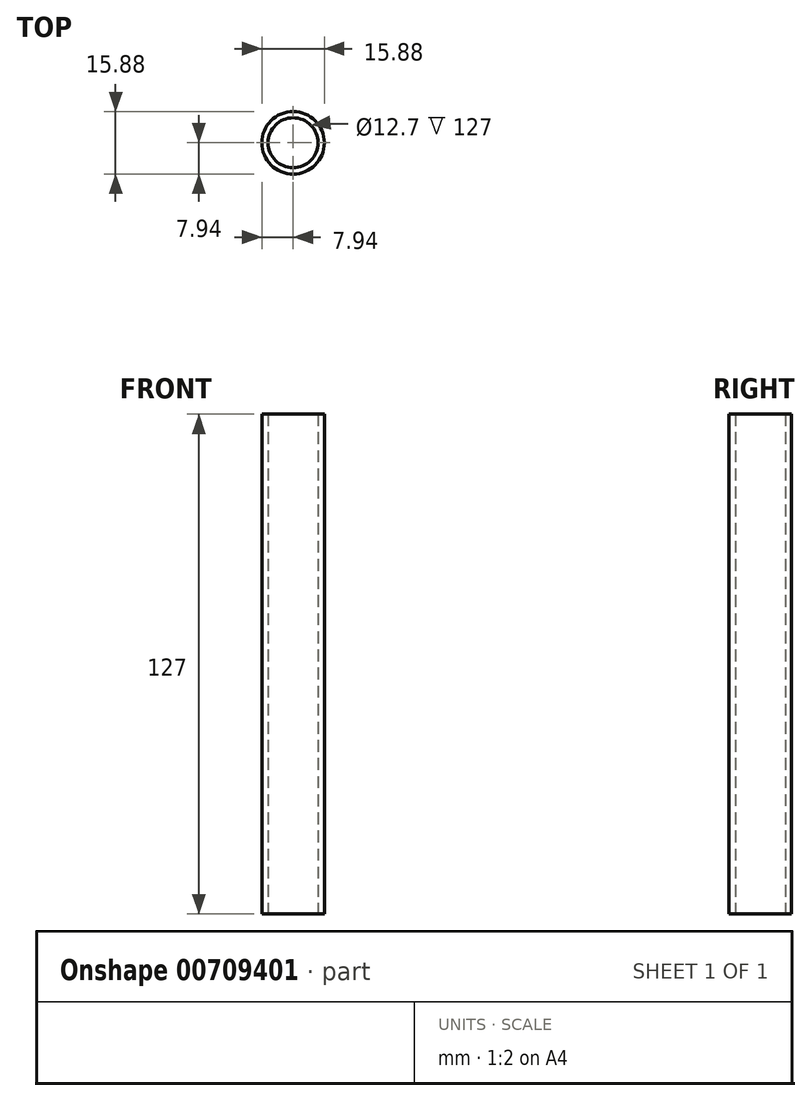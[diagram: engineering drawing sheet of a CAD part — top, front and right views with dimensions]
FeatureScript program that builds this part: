
annotation { "Feature Type Name" : "Feature", "Feature Type Description" : "" }
export const myFeature = defineFeature(function(context is Context, id is Id, definition is map)
    precondition{}
    {
        {
            var Q0;
            Q0=qCreatedBy(makeId("Top.planeOp"),FACE);
            var sketch = newSketch(context, id + "F0", { "sketchPlane" : qUnion([Q0])});
            skLineSegment(sketch, "E0", {"start": v(0, 0) * mm, "end": v(6.35, 0) * mm});
            skCircle(sketch, "E1", {"center": v(0, 0) * mm, "radius": 6.35 * mm});
            skCircle(sketch, "E2.0", {"center": v(0, 0) * mm, "radius": 7.94 * mm});
            skSolve(sketch);
        }
        {
            var Q0;
            Q0=qSketchRegion(id+"FEloJnSHgHgsXCt_0",true);
            var Q1;
            Q1=makeQuery(id+"F0.imprint","IMPRINT",FACE,{"disambiguationData":[TD([[makeQuery(id+"F0.imprint","IMPRINT",EDGE,{"derivedFrom":sQuery(id+"F0.wireOp",EDGE,"E1")}),-1.0]])]});
            extrude(context, id + "F1", {"entities" : qUnion([Q0, Q1]), "depth" : 127 * mm, "offsetDistance" : 25.4 * mm});
        }
    });
